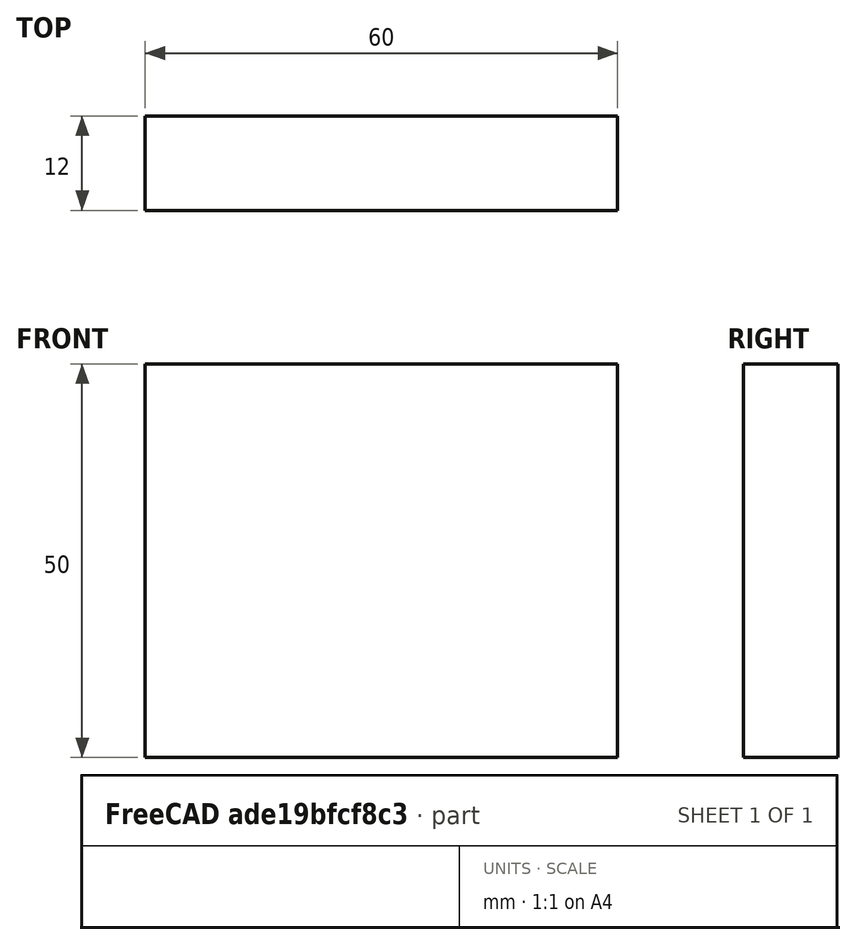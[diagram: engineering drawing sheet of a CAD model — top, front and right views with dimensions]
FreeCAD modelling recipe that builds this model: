
FCSTD DOCUMENT  (FreeCAD 0.15R4671 (Git))
Label: Flat Bar 60x12 EN10058 S235JR
License: All rights reserved
LicenseURL: http://en.wikipedia.org/wiki/All_rights_reserved
objects: Sketcher::SketchObject×1, Part::Extrusion×1
note: 2 computed .brp shape members not serialized (recipe doc carries the construction recipe); baked Part::Feature solids carry a one-line shape summary decoded from their .brp

FEATURE [Sketcher::SketchObject] Sketch
  sketch-geometry (4):
    g0: LineSegment StartX=-30 StartY=-6 StartZ=0 EndX=30 EndY=-6 EndZ=0
    g1: LineSegment StartX=30 StartY=-6 StartZ=0 EndX=30 EndY=6 EndZ=0
    g2: LineSegment StartX=30 StartY=6 StartZ=0 EndX=-30 EndY=6 EndZ=0
    g3: LineSegment StartX=-30 StartY=6 StartZ=0 EndX=-30 EndY=-6 EndZ=0
  constraints (12):
    c: Coincident(g0,g1)
    c: Coincident(g1,g2)
    c: Coincident(g2,g3)
    c: Coincident(g3,g0)
    c: Horizontal(g0)
    c: Horizontal(g2)
    c: Vertical(g1)
    c: Vertical(g3)
    c: Symmetric(g1,g2,g-2)
    c: Symmetric(g0,g1,g-1)
    c: DistanceY(g1) = 12
    c: DistanceX(g0) = 60
FEATURE [Part::Extrusion] Extrude  label="Flat Bar 60x12 EN10058 S235JR"
  Base = -> Sketch
  Dir = (0,0,50)
  Solid = true
